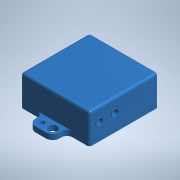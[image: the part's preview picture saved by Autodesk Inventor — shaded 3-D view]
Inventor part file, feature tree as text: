
AUTODESK INVENTOR PART (.ipt)
format: ipt  version: 2022.1 (Build 261234000, 234)  size: 185,856 bytes
history: native  units: mm (DEFAULTED — no unit token found)
features: other x8, extrude x4, sketch x4, fillet x2
bodies: Body1 (feature_tree)
feature tree (18):
  other  "Sólido1"
  other  "Origen"
  extrude  "Extrusión1"  Depth=25.4mm
  extrude  "Extrusión2"  Depth=5.2578mm
  sketch  "Boceto3"  dims[d7=3.175mm d8=1.6002mm]
  fillet  "Empalme1"  Radius=5.2578mm
  fillet  "Empalme2"  Radius=3.175mm
  extrude  "Extrusión3"  Depth=1.6002mm
  extrude  "Extrusión4"  Depth=0.3556mm
  other  "Plano YZ"
  other  "Plano XZ"
  other  "Plano XY"
  other  "Eje X"
  other  "Eje Y"
  other  "Eje Z"
  sketch  "Boceto1"  dims[d0=25.4mm d1=25.4mm]
  sketch  "Boceto2"  dims[d2=11.176mm d3=0.0mm d4=5.2578mm d5=5.2578mm d6=3.175mm]
  sketch  "Boceto4"  dims[d9=1.6002mm d12=30.8356mm d13=1.905mm d14=1.905mm d15=3.81mm d16=3.81mm d17=3.81mm d18=3.81mm d19=1.905mm d20=0.0mm d21=0.9525mm d22=0.9525mm d23=3.7084mm d24=9.2964mm d25=6.477mm d26=6.477mm d27=2.413mm d28=2.6924mm d29=0.0mm d30=2.54mm d31=0.3556mm d32=0.0mm]
